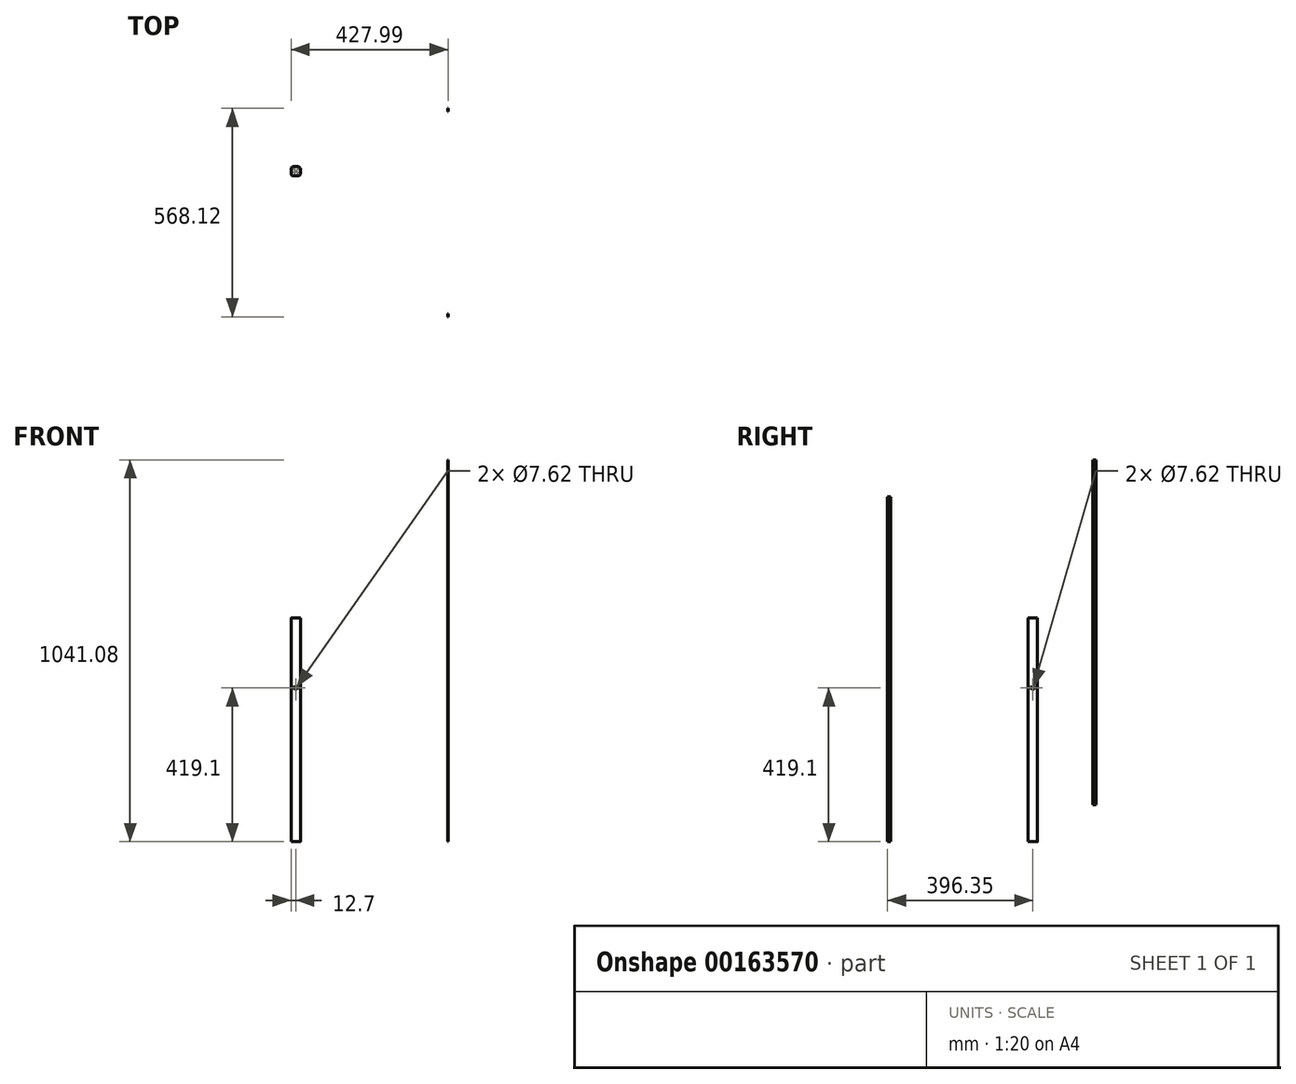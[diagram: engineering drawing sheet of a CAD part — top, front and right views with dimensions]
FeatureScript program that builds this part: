
annotation { "Feature Type Name" : "Feature", "Feature Type Description" : "" }
export const myFeature = defineFeature(function(context is Context, id is Id, definition is map)
    precondition{}
    {
        {
            var Q0;
            Q0=qCreatedBy(makeId("Top.planeOp"),FACE);
            var sketch = newSketch(context, id + "F0", { "sketchPlane" : qUnion([Q0])});
            skLineSegment(sketch, "E0.bottom", {"start": v(6.35, 12.7) * mm, "end": v(-6.35, 12.7) * mm});
            skLineSegment(sketch, "E0.top", {"start": v(6.35, -12.7) * mm, "end": v(-6.35, -12.7) * mm});
            skLineSegment(sketch, "E0.left", {"start": v(12.7, 6.35) * mm, "end": v(12.7, -6.35) * mm});
            skLineSegment(sketch, "E0.right", {"start": v(-12.7, 6.35) * mm, "end": v(-12.7, -6.35) * mm});
            skPoint(sketch, "E0.middle", {"position": v(0, 0) * mm});
            skPoint(sketch, "E1.visualSharp", {"position": v(-12.7, 12.7) * mm});
            skArc(sketch, "E1.filletArc", {"start": v(-6.35, 12.7) * mm, "mid": v(-10.84, 10.84) * mm, "end": v(-12.7, 6.35) * mm});
            skPoint(sketch, "E2.visualSharp", {"position": v(-12.7, -12.7) * mm});
            skArc(sketch, "E2.filletArc", {"start": v(-12.7, -6.35) * mm, "mid": v(-10.84, -10.84) * mm, "end": v(-6.35, -12.7) * mm});
            skPoint(sketch, "E3.visualSharp", {"position": v(12.7, -12.7) * mm});
            skArc(sketch, "E3.filletArc", {"start": v(6.35, -12.7) * mm, "mid": v(10.84, -10.84) * mm, "end": v(12.7, -6.35) * mm});
            skPoint(sketch, "E4.visualSharp", {"position": v(12.7, 12.7) * mm});
            skArc(sketch, "E4.filletArc", {"start": v(12.7, 6.35) * mm, "mid": v(10.84, 10.84) * mm, "end": v(6.35, 12.7) * mm});
            skSolve(sketch);
        }
        {
            var Q0;
            Q0=qSketchRegion(id+"F0",true);
            extrude(context, id + "F1", {"entities" : qUnion([Q0]), "depth" : 609.6 * mm});
        }
        {
            var Q0;
            Q0=qCreatedBy(makeId("Right.planeOp"),FACE);
            var sketch = newSketch(context, id + "F2", { "sketchPlane" : qUnion([Q0])});
            skLineSegment(sketch, "E5.bottom", {"start": v(-396.35, 939.8) * mm, "end": v(-387.88, 939.8) * mm});
            skLineSegment(sketch, "E5.top", {"start": v(-396.35, 0) * mm, "end": v(-387.88, 0) * mm});
            skLineSegment(sketch, "E5.left", {"start": v(-396.35, 939.8) * mm, "end": v(-396.35, 0) * mm});
            skLineSegment(sketch, "E5.right", {"start": v(-387.88, 939.8) * mm, "end": v(-387.88, 0) * mm});
            skSolve(sketch);
        }
        {
            var Q0;
            Q0=qSketchRegion(id+"F2",true);
            extrude(context, id + "F3", {"entities" : qUnion([Q0]), "depth" : 1.27 * mm});
        }
        {
            var Q0;
            Q0=qCreatedBy(makeId("Right.planeOp"),FACE);
            var sketch = newSketch(context, id + "F4", { "sketchPlane" : qUnion([Q0])});
            skLineSegment(sketch, "E6.bottom", {"start": v(163.3, 1041.08) * mm, "end": v(171.77, 1041.08) * mm});
            skLineSegment(sketch, "E6.top", {"start": v(163.3, 101.28) * mm, "end": v(171.77, 101.28) * mm});
            skLineSegment(sketch, "E6.left", {"start": v(163.3, 1041.08) * mm, "end": v(163.3, 101.28) * mm});
            skLineSegment(sketch, "E6.right", {"start": v(171.77, 1041.08) * mm, "end": v(171.77, 101.28) * mm});
            skSolve(sketch);
        }
        {
            var Q0;
            Q0=qSketchRegion(id+"F4",true);
            extrude(context, id + "F5", {"entities" : qUnion([Q0]), "depth" : 1.27 * mm});
        }
        {
            var Q0;
            Q0=makeQuery(id+"F5.opExtrude","SWEPT_BODY",BODY,{"disambiguationData":[OSD([sQuery(id+"F4.wireOp",EDGE,"E6.bottom"),sQuery(id+"F4.wireOp",EDGE,"E6.top"),sQuery(id+"F4.wireOp",EDGE,"E6.left"),sQuery(id+"F4.wireOp",EDGE,"E6.right")])]});
            var Q1;
            Q1=makeQuery(id+"F3.opExtrude","SWEPT_BODY",BODY,{"disambiguationData":[OSD([sQuery(id+"F2.wireOp",EDGE,"E5.bottom"),sQuery(id+"F2.wireOp",EDGE,"E5.top"),sQuery(id+"F2.wireOp",EDGE,"E5.left"),sQuery(id+"F2.wireOp",EDGE,"E5.right")])]});
            transform(context, id + "F6", {"entities" : qUnion([Q0, Q1]), "transformType" : TransformType.TRANSLATION_3D, "dx" : 414.02 * mm, "dy" : 0 * mm, "dz" : 0 * mm, "makeCopy" : false});
        }
        {
            var Q0;
            Q0=makeQuery(id+"F1.opExtrude","SWEPT_FACE",FACE,{"disambiguationData":[OSD([sQuery(id+"F0.wireOp",EDGE,"E0.right")])]});
            var sketch = newSketch(context, id + "F7", { "sketchPlane" : qUnion([Q0])});
            skPoint(sketch, "E7.endSnap0", {"position": v(0, 609.6) * mm});
            skCircle(sketch, "E8", {"center": v(0, 596.9) * mm, "radius": 3.81 * mm});
            skPoint(sketch, "E9.endSnap0", {"position": v(0, 0) * mm});
            skCircle(sketch, "E10", {"center": v(0, 419.1) * mm, "radius": 3.81 * mm});
            skSolve(sketch);
        }
        {
            var Q0;
            Q0=makeQuery(id+"F7.imprint","IMPRINT",FACE,{"disambiguationData":[TD([[makeQuery(id+"F7.imprint","IMPRINT",EDGE,{"derivedFrom":sQuery(id+"F7.wireOp",EDGE,"E10")}),1.0]])]});
            extrude(context, id + "F8", {"entities" : qUnion([Q0]), "operationType" : NewBodyOperationType.REMOVE, "oppositeDirection" : true, "depth" : 25.4 * mm});
        }
        {
            var Q0;
            Q0=makeQuery(id+"F1.opExtrude","SWEPT_FACE",FACE,{"disambiguationData":[OSD([sQuery(id+"F0.wireOp",EDGE,"E0.top")])]});
            var sketch = newSketch(context, id + "F9", { "sketchPlane" : qUnion([Q0])});
            skLineSegment(sketch, "E11", {"start": v(0, 0) * mm, "end": v(0, 419.1) * mm});
            skCircle(sketch, "E12", {"center": v(0, 419.1) * mm, "radius": 3.81 * mm});
            skSolve(sketch);
        }
        {
            var Q0;
            Q0=makeQuery(id+"F9.imprint","IMPRINT",FACE,{"disambiguationData":[TD([[makeQuery(id+"F9.imprint","IMPRINT",EDGE,{"derivedFrom":sQuery(id+"F9.wireOp",EDGE,"E12")}),1.0]])]});
            extrude(context, id + "F10", {"entities" : qUnion([Q0]), "operationType" : NewBodyOperationType.REMOVE, "oppositeDirection" : true, "depth" : 25.4 * mm});
        }
    });
